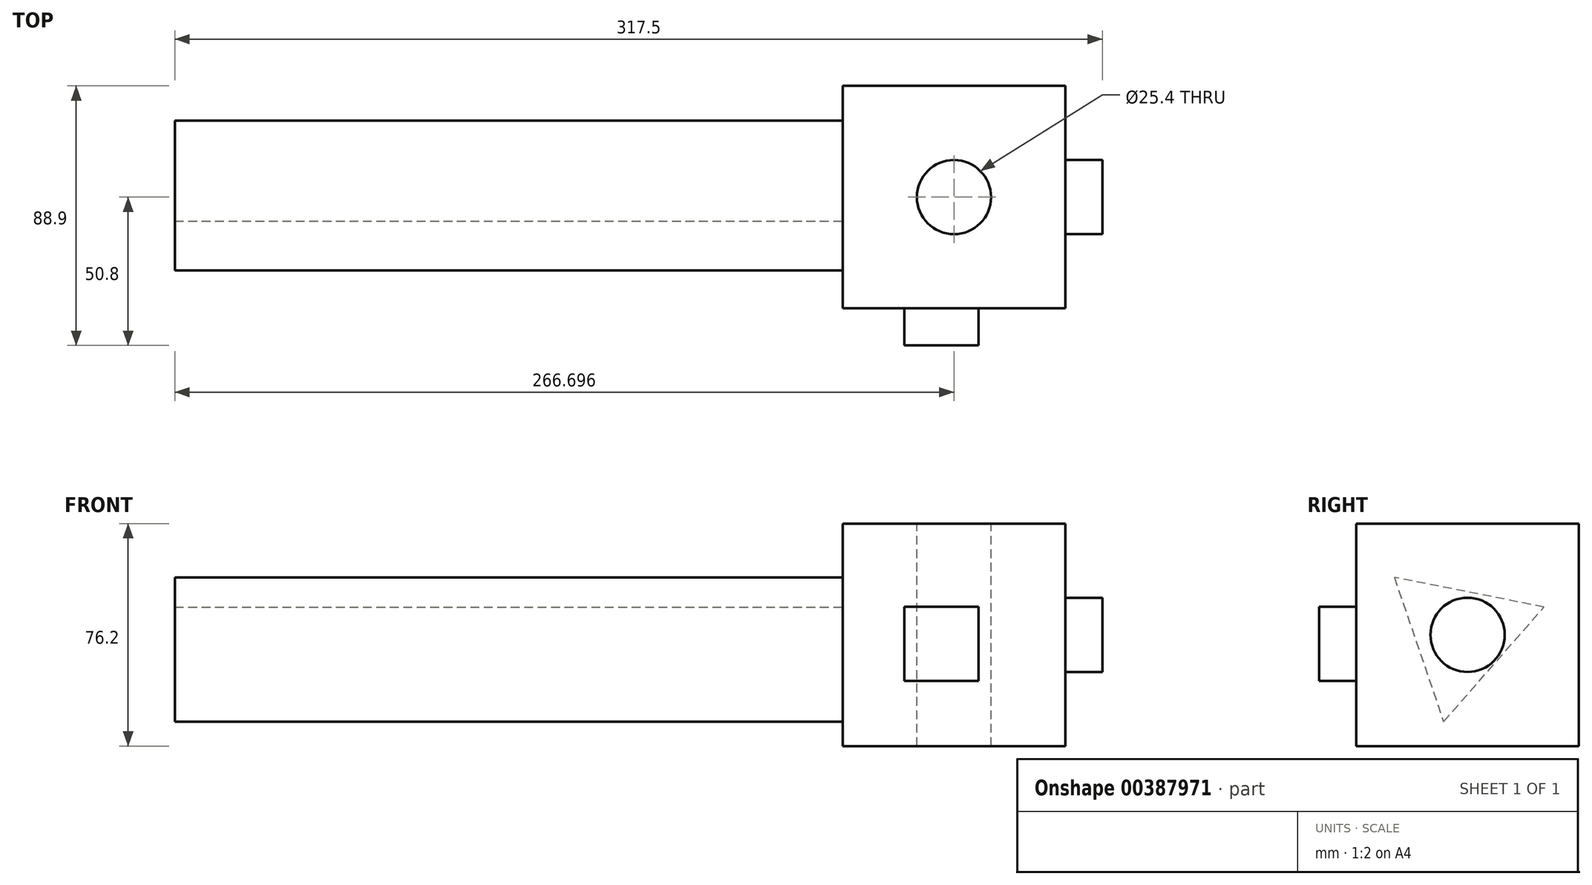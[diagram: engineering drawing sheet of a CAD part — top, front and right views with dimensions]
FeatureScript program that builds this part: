
annotation { "Feature Type Name" : "Feature", "Feature Type Description" : "" }
export const myFeature = defineFeature(function(context is Context, id is Id, definition is map)
    precondition{}
    {
        {
            var Q0;
            Q0=qCreatedBy(makeId("Front.planeOp"),FACE);
            var sketch = newSketch(context, id + "F0", { "sketchPlane" : qUnion([Q0])});
            skLineSegment(sketch, "E0.bottom", {"start": v(-35.73, -37.32) * mm, "end": v(40.47, -37.32) * mm});
            skLineSegment(sketch, "E0.top", {"start": v(-35.73, 38.88) * mm, "end": v(40.47, 38.88) * mm});
            skLineSegment(sketch, "E0.left", {"start": v(-35.73, -37.32) * mm, "end": v(-35.73, 38.88) * mm});
            skLineSegment(sketch, "E0.right", {"start": v(40.47, -37.32) * mm, "end": v(40.47, 38.88) * mm});
            skSolve(sketch);
        }
        {
            var Q0;
            Q0 = qSketchRegion(id + "F0", true);
            extrude(context, id + "F1", {"entities" : qUnion([Q0]), "depth" : 76.2 * mm});
        }
        {
            var Q0;
            Q0=makeQuery(id+"F1.opExtrude","SWEPT_FACE",FACE,{"disambiguationData":[OSD([sQuery(id+"F0.wireOp",EDGE,"E0.top")])]});
            var sketch = newSketch(context, id + "F2", { "sketchPlane" : qUnion([Q0])});
            skPoint(sketch, "E1", {"position": v(2.37, -38.1) * mm});
            skSolve(sketch);
        }
        {
            var Q0;
            Q0=makeQuery(id+"F1.opExtrude","CAP_FACE",FACE,{"disambiguationData":[OSD([sQuery(id+"F0.wireOp",EDGE,"E0.bottom"),sQuery(id+"F0.wireOp",EDGE,"E0.top"),sQuery(id+"F0.wireOp",EDGE,"E0.left"),sQuery(id+"F0.wireOp",EDGE,"E0.right")])],"isStart":false});
            var sketch = newSketch(context, id + "F3", { "sketchPlane" : qUnion([Q0])});
            skLineSegment(sketch, "E2.bottom", {"start": v(-14.6, -15) * mm, "end": v(10.8, -15) * mm});
            skLineSegment(sketch, "E2.top", {"start": v(-14.6, 10.4) * mm, "end": v(10.8, 10.4) * mm});
            skLineSegment(sketch, "E2.left", {"start": v(-14.6, -15) * mm, "end": v(-14.6, 10.4) * mm});
            skLineSegment(sketch, "E2.right", {"start": v(10.8, -15) * mm, "end": v(10.8, 10.4) * mm});
            skSolve(sketch);
        }
        {
            var Q0;
            Q0=sQuery(id+"F2.wireOp",VERTEX,"E1");
            var Q1;
            Q1=makeQuery(id+"F1.opExtrude","SWEPT_BODY",BODY,{"disambiguationData":[OSD([sQuery(id+"F0.wireOp",EDGE,"E0.bottom"),sQuery(id+"F0.wireOp",EDGE,"E0.top"),sQuery(id+"F0.wireOp",EDGE,"E0.left"),sQuery(id+"F0.wireOp",EDGE,"E0.right")])]});
            hole(context, id + "F4", {"style" : HoleStyle.SIMPLE, "endStyle" : HoleEndStyle.THROUGH, "holeDiameter" : 25.4 * mm, "isTappedThrough" : true, "tappedDepth" : 12.7 * mm, "tapClearance" : 3, "locations" : qUnion([Q0]), "scope" : qUnion([Q1])});
        }
        {
            var Q0;
            Q0 = qSketchRegion(id + "F3", true);
            extrude(context, id + "F5", {"entities" : qUnion([Q0]), "operationType" : NewBodyOperationType.ADD, "depth" : 12.7 * mm});
        }
        {
            var Q0;
            Q0=makeQuery(id+"F1.opExtrude","SWEPT_FACE",FACE,{"disambiguationData":[OSD([sQuery(id+"F0.wireOp",EDGE,"E0.right")])]});
            var sketch = newSketch(context, id + "F6", { "sketchPlane" : qUnion([Q0])});
            skCircle(sketch, "E3", {"center": v(-38.1, 0.78) * mm, "radius": 12.7 * mm});
            skSolve(sketch);
        }
        {
            var Q0;
            Q0=makeQuery(id+"F6.imprint","IMPRINT",FACE,{"disambiguationData":[TD([[makeQuery(id+"F6.imprint","IMPRINT",EDGE,{"derivedFrom":sQuery(id+"F6.wireOp",EDGE,"E3")}),1.0]])]});
            extrude(context, id + "F7", {"entities" : qUnion([Q0]), "operationType" : NewBodyOperationType.ADD, "depth" : 12.7 * mm});
        }
        {
            var Q0;
            Q0=makeQuery(id+"F1.opExtrude","SWEPT_FACE",FACE,{"disambiguationData":[OSD([sQuery(id+"F0.wireOp",EDGE,"E0.left")])]});
            var sketch = newSketch(context, id + "F8", { "sketchPlane" : qUnion([Q0])});
            skCircle(sketch, "E4.cCircle", {"center": v(40.46, 0.58) * mm, "radius": 15.07 * mm, "construction": true});
            skLineSegment(sketch, "E4.0", {"start": v(46.3, -28.98) * mm, "end": v(11.94, 10.31) * mm});
            skLineSegment(sketch, "E4.1", {"start": v(11.94, 10.31) * mm, "end": v(63.15, 20.42) * mm});
            skLineSegment(sketch, "E4.2", {"start": v(63.15, 20.42) * mm, "end": v(46.3, -28.98) * mm});
            skPoint(sketch, "E4.0.midPoint", {"position": v(29.12, -9.34) * mm});
            skSolve(sketch);
        }
        {
            var Q0;
            Q0 = qSketchRegion(id + "F8", true);
            extrude(context, id + "F9", {"entities" : qUnion([Q0]), "operationType" : NewBodyOperationType.ADD, "depth" : 228.6 * mm});
        }
    });
